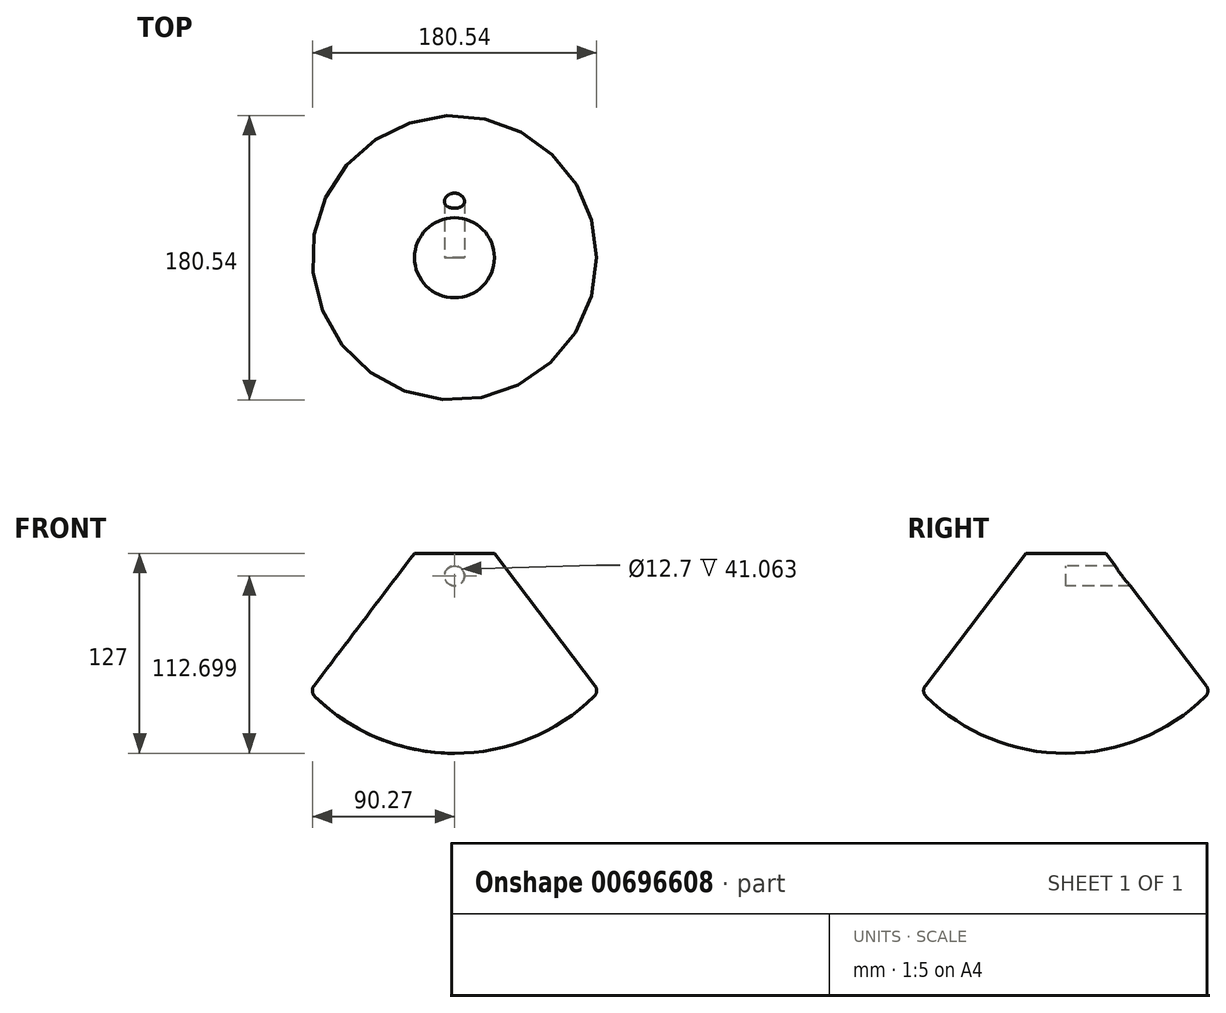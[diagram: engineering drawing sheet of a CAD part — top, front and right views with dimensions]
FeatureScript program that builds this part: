
annotation { "Feature Type Name" : "Feature", "Feature Type Description" : "" }
export const myFeature = defineFeature(function(context is Context, id is Id, definition is map)
    precondition{}
    {
        {
            var Q0;
            Q0=qCreatedBy(makeId("Front.planeOp"),FACE);
            var sketch = newSketch(context, id + "F0", { "sketchPlane" : qUnion([Q0])});
            skLineSegment(sketch, "E0", {"start": v(0, 0) * mm, "end": v(0, 127) * mm});
            skLineSegment(sketch, "E1", {"start": v(0, 127) * mm, "end": v(-25.4, 127) * mm});
            skLineSegment(sketch, "E2", {"start": v(-25.4, 127) * mm, "end": v(-91.9, 39.35) * mm});
            skArc(sketch, "E3", {"start": v(-91.9, 39.35) * mm, "mid": v(-49.98, 10.25) * mm, "end": v(0, 0) * mm});
            skSolve(sketch);
        }
        {
            var Q0;
            Q0=makeQuery(id+"F0.imprint","IMPRINT",FACE,{"disambiguationData":[TD([[makeQuery(id+"F0.imprint","IMPRINT",EDGE,{"derivedFrom":sQuery(id+"F0.wireOp",EDGE,"E0")}),1.0]])]});
            var Q1;
            Q1=sQuery(id+"F0.wireOp",EDGE,"E0");
            revolve(context, id + "F1", {"entities" : qUnion([Q0]), "axis" : qUnion([Q1]), "revolveType" : RevolveType.FULL});
        }
        {
            var Q0;
            Q0=makeQuery(id+"F1.opRevolve","SWEPT_EDGE",EDGE,{"disambiguationData":[OSD([sQuery(id+"F0.wireOp",EDGE,"E2"),sQuery(id+"F0.wireOp",EDGE,"E3")])]});
            fillet(context, id + "F2", {"entities" : qUnion([Q0]), "radius" : 5.08 * mm, "tangentPropagation" : true, "allowEdgeOverflow" : false});
        }
        {
            var Q0;
            Q0=qCreatedBy(makeId("Front.planeOp"),FACE);
            var sketch = newSketch(context, id + "F3", { "sketchPlane" : qUnion([Q0])});
            skCircle(sketch, "E4", {"center": v(0, 112.7) * mm, "radius": 7.65 * mm});
            skSolve(sketch);
        }
        {
            var Q0;
            Q0=sQuery(id+"F3.wireOp",VERTEX,"E4.center");
            var Q1;
            Q1=makeQuery(id+"F1.opRevolve","SWEPT_BODY",BODY,{"disambiguationData":[OSD([sQuery(id+"F0.wireOp",EDGE,"E0"),sQuery(id+"F0.wireOp",EDGE,"E1"),sQuery(id+"F0.wireOp",EDGE,"E2"),sQuery(id+"F0.wireOp",EDGE,"E3")])]});
            hole(context, id + "F4", {"style" : HoleStyle.SIMPLE, "endStyle" : HoleEndStyle.THROUGH, "holeDiameter" : 12.7 * mm, "majorDiameter" : 6.35 * mm, "isTappedThrough" : true, "tappedDepth" : 12.7 * mm, "tapClearance" : 3, "startFromSketch" : true, "locations" : qUnion([Q0]), "scope" : qUnion([Q1])});
        }
    });
